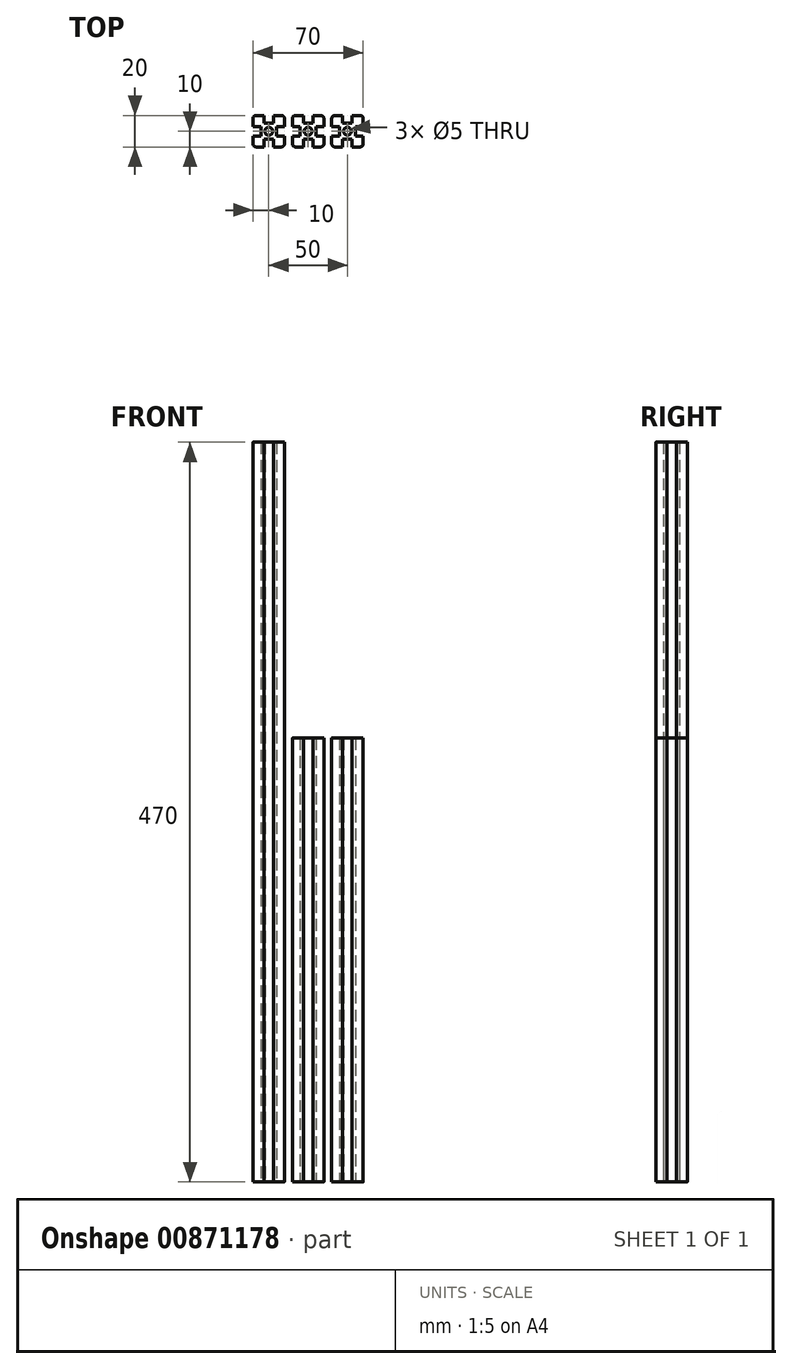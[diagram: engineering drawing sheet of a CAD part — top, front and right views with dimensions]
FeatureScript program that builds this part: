
annotation { "Feature Type Name" : "Feature", "Feature Type Description" : "" }
export const myFeature = defineFeature(function(context is Context, id is Id, definition is map)
    precondition{}
    {
        {
            var Q0;
            Q0=qCreatedBy(makeId("Top.planeOp"),FACE);
            var sketch = newSketch(context, id + "F0", { "sketchPlane" : qUnion([Q0])});
            skLineSegment(sketch, "E0.bottom", {"start": v(8, 10) * mm, "end": v(3, 10) * mm});
            skLineSegment(sketch, "E0.top", {"start": v(8, -10) * mm, "end": v(3, -10) * mm});
            skLineSegment(sketch, "E0.left", {"start": v(10, 8) * mm, "end": v(10, 3) * mm});
            skLineSegment(sketch, "E0.right", {"start": v(-10, 8) * mm, "end": v(-10, 3) * mm});
            skPoint(sketch, "E0.middle", {"position": v(0, 0) * mm});
            skLineSegment(sketch, "E1.top", {"start": v(-3, 5) * mm, "end": v(3, 5) * mm});
            skLineSegment(sketch, "E1.left", {"start": v(-3, 10) * mm, "end": v(-3, 5) * mm});
            skLineSegment(sketch, "E1.right", {"start": v(3, 10) * mm, "end": v(3, 5) * mm});
            skLineSegment(sketch, "E2.trimOffspring", {"start": v(-3, 10) * mm, "end": v(-8, 10) * mm});
            skPoint(sketch, "E3", {"position": v(0, 10) * mm});
            skLineSegment(sketch, "E4.1.0", {"start": v(-10, -3) * mm, "end": v(-5, -3) * mm});
            skLineSegment(sketch, "E4.1.1", {"start": v(-5, -3) * mm, "end": v(-5, 3) * mm});
            skLineSegment(sketch, "E4.1.2", {"start": v(-10, 3) * mm, "end": v(-5, 3) * mm});
            skLineSegment(sketch, "E4.2.0", {"start": v(3, -10) * mm, "end": v(3, -5) * mm});
            skLineSegment(sketch, "E4.2.1", {"start": v(3, -5) * mm, "end": v(-3, -5) * mm});
            skLineSegment(sketch, "E4.2.2", {"start": v(-3, -10) * mm, "end": v(-3, -5) * mm});
            skLineSegment(sketch, "E4.3.0", {"start": v(10, 3) * mm, "end": v(5, 3) * mm});
            skLineSegment(sketch, "E4.3.1", {"start": v(5, 3) * mm, "end": v(5, -3) * mm});
            skLineSegment(sketch, "E4.3.2", {"start": v(10, -3) * mm, "end": v(5, -3) * mm});
            skLineSegment(sketch, "E5.trimOffspring", {"start": v(10, -3) * mm, "end": v(10, -8) * mm});
            skLineSegment(sketch, "E6.trimOffspring", {"start": v(-3, -10) * mm, "end": v(-8, -10) * mm});
            skLineSegment(sketch, "E7.trimOffspring", {"start": v(-10, -3) * mm, "end": v(-10, -8) * mm});
            skPoint(sketch, "E8.visualSharp", {"position": v(-10, 10) * mm});
            skArc(sketch, "E8.filletArc", {"start": v(-8, 10) * mm, "mid": v(-9.41, 9.41) * mm, "end": v(-10, 8) * mm});
            skPoint(sketch, "E9.visualSharp", {"position": v(10, 10) * mm});
            skArc(sketch, "E9.filletArc", {"start": v(10, 8) * mm, "mid": v(9.41, 9.41) * mm, "end": v(8, 10) * mm});
            skPoint(sketch, "E10.visualSharp", {"position": v(10, -10) * mm});
            skArc(sketch, "E10.filletArc", {"start": v(8, -10) * mm, "mid": v(9.41, -9.41) * mm, "end": v(10, -8) * mm});
            skPoint(sketch, "E11.visualSharp", {"position": v(-10, -10) * mm});
            skArc(sketch, "E11.filletArc", {"start": v(-10, -8) * mm, "mid": v(-9.41, -9.41) * mm, "end": v(-8, -10) * mm});
            skLineSegment(sketch, "E12.1.0.0", {"start": v(15, -3) * mm, "end": v(15, -8) * mm});
            skPoint(sketch, "E12.1.0.1", {"position": v(25, 10) * mm});
            skLineSegment(sketch, "E12.1.0.2", {"start": v(28, -5) * mm, "end": v(22, -5) * mm});
            skPoint(sketch, "E12.1.0.3", {"position": v(15, 10) * mm});
            skLineSegment(sketch, "E12.1.0.4", {"start": v(22, 10) * mm, "end": v(17, 10) * mm});
            skPoint(sketch, "E12.1.0.5", {"position": v(35, 10) * mm});
            skLineSegment(sketch, "E12.1.0.6", {"start": v(35, -3) * mm, "end": v(35, -8) * mm});
            skLineSegment(sketch, "E12.1.0.7", {"start": v(20, -3) * mm, "end": v(20, 3) * mm});
            skPoint(sketch, "E12.1.0.8", {"position": v(25, 0) * mm});
            skPoint(sketch, "E12.1.0.9", {"position": v(35, -10) * mm});
            skLineSegment(sketch, "E12.1.0.10", {"start": v(35, 3) * mm, "end": v(30, 3) * mm});
            skLineSegment(sketch, "E12.1.0.11", {"start": v(35, 8) * mm, "end": v(35, 3) * mm});
            skLineSegment(sketch, "E12.1.0.12", {"start": v(22, -10) * mm, "end": v(22, -5) * mm});
            skLineSegment(sketch, "E12.1.0.13", {"start": v(22, 5) * mm, "end": v(28, 5) * mm});
            skLineSegment(sketch, "E12.1.0.14", {"start": v(33, -10) * mm, "end": v(28, -10) * mm});
            skLineSegment(sketch, "E12.1.0.15", {"start": v(15, 3) * mm, "end": v(20, 3) * mm});
            skLineSegment(sketch, "E12.1.0.16", {"start": v(28, 10) * mm, "end": v(28, 5) * mm});
            skLineSegment(sketch, "E12.1.0.17", {"start": v(15, 8) * mm, "end": v(15, 3) * mm});
            skLineSegment(sketch, "E12.1.0.18", {"start": v(22, -10) * mm, "end": v(17, -10) * mm});
            skPoint(sketch, "E12.1.0.19", {"position": v(15, -10) * mm});
            skLineSegment(sketch, "E12.1.0.20", {"start": v(33, 10) * mm, "end": v(28, 10) * mm});
            skLineSegment(sketch, "E12.1.0.21", {"start": v(35, -3) * mm, "end": v(30, -3) * mm});
            skLineSegment(sketch, "E12.1.0.22", {"start": v(30, 3) * mm, "end": v(30, -3) * mm});
            skLineSegment(sketch, "E12.1.0.23", {"start": v(28, -10) * mm, "end": v(28, -5) * mm});
            skLineSegment(sketch, "E12.1.0.24", {"start": v(15, -3) * mm, "end": v(20, -3) * mm});
            skArc(sketch, "E12.1.0.25", {"start": v(35, 8) * mm, "mid": v(34.41, 9.41) * mm, "end": v(33, 10) * mm});
            skLineSegment(sketch, "E12.1.0.26", {"start": v(22, 10) * mm, "end": v(22, 5) * mm});
            skArc(sketch, "E12.1.0.27", {"start": v(15, -8) * mm, "mid": v(15.59, -9.41) * mm, "end": v(17, -10) * mm});
            skArc(sketch, "E12.1.0.28", {"start": v(33, -10) * mm, "mid": v(34.41, -9.41) * mm, "end": v(35, -8) * mm});
            skArc(sketch, "E12.1.0.29", {"start": v(17, 10) * mm, "mid": v(15.59, 9.41) * mm, "end": v(15, 8) * mm});
            skPoint(sketch, "E12.1.0.30", {"position": v(25, 0) * mm});
            skLineSegment(sketch, "E12.2.0.0", {"start": v(40, -3) * mm, "end": v(40, -8) * mm});
            skPoint(sketch, "E12.2.0.1", {"position": v(50, 10) * mm});
            skLineSegment(sketch, "E12.2.0.2", {"start": v(53, -5) * mm, "end": v(47, -5) * mm});
            skPoint(sketch, "E12.2.0.3", {"position": v(40, 10) * mm});
            skLineSegment(sketch, "E12.2.0.4", {"start": v(47, 10) * mm, "end": v(42, 10) * mm});
            skPoint(sketch, "E12.2.0.5", {"position": v(60, 10) * mm});
            skLineSegment(sketch, "E12.2.0.6", {"start": v(60, -3) * mm, "end": v(60, -8) * mm});
            skLineSegment(sketch, "E12.2.0.7", {"start": v(45, -3) * mm, "end": v(45, 3) * mm});
            skPoint(sketch, "E12.2.0.8", {"position": v(50, 0) * mm});
            skPoint(sketch, "E12.2.0.9", {"position": v(60, -10) * mm});
            skLineSegment(sketch, "E12.2.0.10", {"start": v(60, 3) * mm, "end": v(55, 3) * mm});
            skLineSegment(sketch, "E12.2.0.11", {"start": v(60, 8) * mm, "end": v(60, 3) * mm});
            skLineSegment(sketch, "E12.2.0.12", {"start": v(47, -10) * mm, "end": v(47, -5) * mm});
            skLineSegment(sketch, "E12.2.0.13", {"start": v(47, 5) * mm, "end": v(53, 5) * mm});
            skLineSegment(sketch, "E12.2.0.14", {"start": v(58, -10) * mm, "end": v(53, -10) * mm});
            skLineSegment(sketch, "E12.2.0.15", {"start": v(40, 3) * mm, "end": v(45, 3) * mm});
            skLineSegment(sketch, "E12.2.0.16", {"start": v(53, 10) * mm, "end": v(53, 5) * mm});
            skLineSegment(sketch, "E12.2.0.17", {"start": v(40, 8) * mm, "end": v(40, 3) * mm});
            skLineSegment(sketch, "E12.2.0.18", {"start": v(47, -10) * mm, "end": v(42, -10) * mm});
            skPoint(sketch, "E12.2.0.19", {"position": v(40, -10) * mm});
            skLineSegment(sketch, "E12.2.0.20", {"start": v(58, 10) * mm, "end": v(53, 10) * mm});
            skLineSegment(sketch, "E12.2.0.21", {"start": v(60, -3) * mm, "end": v(55, -3) * mm});
            skLineSegment(sketch, "E12.2.0.22", {"start": v(55, 3) * mm, "end": v(55, -3) * mm});
            skLineSegment(sketch, "E12.2.0.23", {"start": v(53, -10) * mm, "end": v(53, -5) * mm});
            skLineSegment(sketch, "E12.2.0.24", {"start": v(40, -3) * mm, "end": v(45, -3) * mm});
            skArc(sketch, "E12.2.0.25", {"start": v(60, 8) * mm, "mid": v(59.41, 9.41) * mm, "end": v(58, 10) * mm});
            skLineSegment(sketch, "E12.2.0.26", {"start": v(47, 10) * mm, "end": v(47, 5) * mm});
            skArc(sketch, "E12.2.0.27", {"start": v(40, -8) * mm, "mid": v(40.59, -9.41) * mm, "end": v(42, -10) * mm});
            skArc(sketch, "E12.2.0.28", {"start": v(58, -10) * mm, "mid": v(59.41, -9.41) * mm, "end": v(60, -8) * mm});
            skArc(sketch, "E12.2.0.29", {"start": v(42, 10) * mm, "mid": v(40.59, 9.41) * mm, "end": v(40, 8) * mm});
            skPoint(sketch, "E12.2.0.30", {"position": v(50, 0) * mm});
            skLineSegment(sketch, "E12.direction1", {"start": v(-10, -10) * mm, "end": v(15, -10) * mm, "construction": true});
            skCircle(sketch, "E13", {"center": v(0, 0) * mm, "radius": 2.5 * mm});
            skCircle(sketch, "E14", {"center": v(25, 0) * mm, "radius": 2.5 * mm});
            skCircle(sketch, "E15", {"center": v(50, 0) * mm, "radius": 2.5 * mm});
            skSolve(sketch);
        }
        {
            var Q0;
            Q0 = qSketchRegion(id + "F0", true);
            extrude(context, id + "F1", {"entities" : qUnion([Q0]), "depth" : 470 * mm, "offsetDistance" : 25 * mm});
        }
        {
            var Q0;
            Q0=makeQuery(id+"F1.opExtrude","CAP_FACE",FACE,{"disambiguationData":[OSD([sQuery(id+"F0.wireOp",EDGE,"E12.1.0.0"),sQuery(id+"F0.wireOp",EDGE,"E12.1.0.2"),sQuery(id+"F0.wireOp",EDGE,"E12.1.0.4"),sQuery(id+"F0.wireOp",EDGE,"E12.1.0.6"),sQuery(id+"F0.wireOp",EDGE,"E12.1.0.7"),sQuery(id+"F0.wireOp",EDGE,"E12.1.0.10"),sQuery(id+"F0.wireOp",EDGE,"E12.1.0.11"),sQuery(id+"F0.wireOp",EDGE,"E12.1.0.12"),sQuery(id+"F0.wireOp",EDGE,"E12.1.0.13"),sQuery(id+"F0.wireOp",EDGE,"E12.1.0.14"),sQuery(id+"F0.wireOp",EDGE,"E12.1.0.15"),sQuery(id+"F0.wireOp",EDGE,"E12.1.0.16"),sQuery(id+"F0.wireOp",EDGE,"E12.1.0.17"),sQuery(id+"F0.wireOp",EDGE,"E12.1.0.18"),sQuery(id+"F0.wireOp",EDGE,"E12.1.0.20"),sQuery(id+"F0.wireOp",EDGE,"E12.1.0.21"),sQuery(id+"F0.wireOp",EDGE,"E12.1.0.22"),sQuery(id+"F0.wireOp",EDGE,"E12.1.0.23"),sQuery(id+"F0.wireOp",EDGE,"E12.1.0.24"),sQuery(id+"F0.wireOp",EDGE,"E12.1.0.25"),sQuery(id+"F0.wireOp",EDGE,"E12.1.0.26"),sQuery(id+"F0.wireOp",EDGE,"E12.1.0.27"),sQuery(id+"F0.wireOp",EDGE,"E12.1.0.28"),sQuery(id+"F0.wireOp",EDGE,"E12.1.0.29")])],"isStart":false});
            var sketch = newSketch(context, id + "F2", { "sketchPlane" : qUnion([Q0])});
            skLineSegment(sketch, "E16.bottom", {"start": v(12, 13.16) * mm, "end": v(37.81, 13.16) * mm});
            skLineSegment(sketch, "E16.top", {"start": v(12, -12.44) * mm, "end": v(37.81, -12.44) * mm});
            skLineSegment(sketch, "E16.left", {"start": v(12, 13.16) * mm, "end": v(12, -12.44) * mm});
            skLineSegment(sketch, "E16.right", {"start": v(37.81, 13.16) * mm, "end": v(37.81, -12.44) * mm});
            skLineSegment(sketch, "E17.bottom", {"start": v(12, -12.44) * mm, "end": v(12.3, -12.44) * mm});
            skLineSegment(sketch, "E17.top", {"start": v(12, -12.44) * mm, "end": v(12.3, -12.44) * mm});
            skLineSegment(sketch, "E17.left", {"start": v(12, -12.44) * mm, "end": v(12, -12.44) * mm});
            skLineSegment(sketch, "E17.right", {"start": v(12.3, -12.44) * mm, "end": v(12.3, -12.44) * mm});
            skSolve(sketch);
        }
        {
            var Q0;
            Q0 = qSketchRegion(id + "F2", true);
            extrude(context, id + "F3", {"entities" : qUnion([Q0]), "operationType" : NewBodyOperationType.REMOVE, "oppositeDirection" : true, "depth" : (110 + 78) * mm, "offsetDistance" : 25 * mm});
        }
        {
            var Q0;
            Q0=makeQuery(id+"F1.opExtrude","CAP_FACE",FACE,{"disambiguationData":[OSD([sQuery(id+"F0.wireOp",EDGE,"E12.2.0.0"),sQuery(id+"F0.wireOp",EDGE,"E12.2.0.2"),sQuery(id+"F0.wireOp",EDGE,"E12.2.0.4"),sQuery(id+"F0.wireOp",EDGE,"E12.2.0.6"),sQuery(id+"F0.wireOp",EDGE,"E12.2.0.7"),sQuery(id+"F0.wireOp",EDGE,"E12.2.0.10"),sQuery(id+"F0.wireOp",EDGE,"E12.2.0.11"),sQuery(id+"F0.wireOp",EDGE,"E12.2.0.12"),sQuery(id+"F0.wireOp",EDGE,"E12.2.0.13"),sQuery(id+"F0.wireOp",EDGE,"E12.2.0.14"),sQuery(id+"F0.wireOp",EDGE,"E12.2.0.15"),sQuery(id+"F0.wireOp",EDGE,"E12.2.0.16"),sQuery(id+"F0.wireOp",EDGE,"E12.2.0.17"),sQuery(id+"F0.wireOp",EDGE,"E12.2.0.18"),sQuery(id+"F0.wireOp",EDGE,"E12.2.0.20"),sQuery(id+"F0.wireOp",EDGE,"E12.2.0.21"),sQuery(id+"F0.wireOp",EDGE,"E12.2.0.22"),sQuery(id+"F0.wireOp",EDGE,"E12.2.0.23"),sQuery(id+"F0.wireOp",EDGE,"E12.2.0.24"),sQuery(id+"F0.wireOp",EDGE,"E12.2.0.25"),sQuery(id+"F0.wireOp",EDGE,"E12.2.0.26"),sQuery(id+"F0.wireOp",EDGE,"E12.2.0.27"),sQuery(id+"F0.wireOp",EDGE,"E12.2.0.28"),sQuery(id+"F0.wireOp",EDGE,"E12.2.0.29")])],"isStart":false});
            var sketch = newSketch(context, id + "F4", { "sketchPlane" : qUnion([Q0])});
            skLineSegment(sketch, "E18.bottom", {"start": v(38.11, 13.86) * mm, "end": v(62.27, 13.86) * mm});
            skLineSegment(sketch, "E18.top", {"start": v(38.11, -11.61) * mm, "end": v(62.27, -11.61) * mm});
            skLineSegment(sketch, "E18.left", {"start": v(38.11, 13.86) * mm, "end": v(38.11, -11.61) * mm});
            skLineSegment(sketch, "E18.right", {"start": v(62.27, 13.86) * mm, "end": v(62.27, -11.61) * mm});
            skSolve(sketch);
        }
        {
            var Q0;
            Q0 = qSketchRegion(id + "F4", true);
            extrude(context, id + "F5", {"entities" : qUnion([Q0]), "operationType" : NewBodyOperationType.REMOVE, "oppositeDirection" : true, "depth" : (110 + 78) * mm, "offsetDistance" : 25 * mm});
        }
    });
